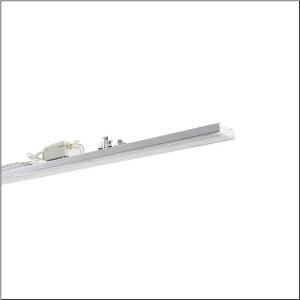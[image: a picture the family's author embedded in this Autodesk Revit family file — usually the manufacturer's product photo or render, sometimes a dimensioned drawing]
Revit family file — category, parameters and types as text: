
# Revit family: licross_21_recessed_ho_52te11mn4fxs
name_source: partatom
category: Lighting Fixtures
units: mm (PartAtom-declared; Revit-internal decimal feet)

## family parameters
Cut with Voids When Loaded = No
Host = Face
Light Source = No
Part Type = Normal
Room Calculation Point = No
Round Connector Dimension = Use Diameter
Shared = No

## types (1)
- --- (1 x LED, 15070 lm, 83.1 W, 4000K)
    Apparent Load = 83 VA
    CIE Flux Codes = 87 95 99 100 100
    Color Rendering = 80
    Color Temperature = 4000K
    Default Elevation = 1800 mm
    Description = Licross 21 Recessed HO, luminaire insert, of sheet steel, galvanised, coil coated, white, length: 1.500mm, width: 66mm, height: 67mm, LED rated luminous flux: 15.060lm, light colour: 840, SDCM (Standard Deviation of Colour Matching)MacAdam ≤ 3 SDCM (initial), control gear: ON/OFF Multilumen, with plug, 3-pole, with phase selection, mains connection: 220..240V, AC, 50/60Hz, rated input power: 83W, internal wiring halogen-free, primary light control with lens, of plastic, primary optical cover: cover, of PMMA, light emission: direct distribution, primary light characteristic: symmetric, protection rating (complete): IP54, insulation class (complete): insulation class I (protective earthing), certification: CE, ENEC, VDE, UKCA, protection symbol: D if used in an environment with non-conductive dust loads with corresponding accessories, impact resistance: IK06, permissible ambient temperature for indoor applications: -35..+30°C, corresponds to IFS (International Featured Standards) requirements for safety and quality in the food industry, reducing of maximum allowable ambient temperature of 5°C with ceiling mounting, LABS conformity tested according to VDMA 24364:2018-05, The light source and the operating device comply with the requirements of the Ecodesign Regulation (EU) 2019/2020 and are replaceable in accordance with this regulation, packaging unit: 1 piece
    Height = 58 mm
    Lamp = 1 x LED
    Lamp Light Flux = 15070 lm
    Lamp Power = 83.1 W
    Lamp count = 1
    Length = 1500 mm
    Luminous efficacy = 181 lm/W
    Manufacturer = Siteco
    ModVariant = No
    Model = 52TE11MN4FXS
    Mounting Place = Ceiling
    Mounting Type = Pendant
    Number of Poles = 1
    OnlyDefault = Yes
    Power Factor = 1
    Product Name = Licross 21 Recessed HO
    Product group = luminaire insert | ceiling pendant
    ProductGroupID = 901
    Protection Class = Protection class I
    Protection Degree = IP 54
    RLX_Detail_Level = 1
    RLX_Emergency_Light_Flux = 0 lm
    RLX_Emergency_Type = 0
    RLX_Emergency_Type_DB = No
    RlxData = <blob elided: 22469 chars, md5=9e616085>
    Socket = socket
    Standby Power = 0 W
    System Light Flux = 15070 lm
    System Power = 83 W
    Type Comments = factory setting: luminous flux: 100 % | (A | C | E) | 195 mA
    Type Image = l_1296930.jpg
    URL = http://relux.com
    VarID = @adj_109551
    Voltage = 0 V
    Weight = 0.00 kg
    Width = 66 mm

## geometry (parser evidence)
native form markers: Blend x4, Sweep x10
no freeform markers — native parametric forms only
